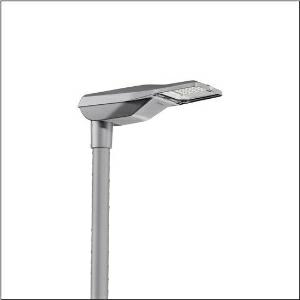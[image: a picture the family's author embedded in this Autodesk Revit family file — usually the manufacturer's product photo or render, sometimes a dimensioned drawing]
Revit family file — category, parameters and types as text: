
# Revit family: streetlight_sl_21_iq_micro___p0_8ab_5xe1r31d08db_6a63
name_source: partatom
category: Lighting Fixtures
units: mm (PartAtom-declared; Revit-internal decimal feet)

## family parameters
Cut with Voids When Loaded = No
Host = Face
Light Source = No
Part Type = Normal
Room Calculation Point = No
Round Connector Dimension = Use Diameter
Shared = No

## types (1)
- --- (1 x LED, 4220 lm, 36.4 W, 3000K)
    Apparent Load = 36 VA
    CIE Flux Codes = 36 71 98 100 100
    Color Rendering = 70
    Color Temperature = 3000K
    Default Elevation = 1800 mm
    Description = Streetlight SL 21 iQ micro, mast luminaire, primary light control with lens, of PMMA, primary optical cover: cover, of toughened safety glass, transparent, light distribution: P0.8aB, light emission: direct distribution, primary light characteristic: asymmetric, installation type: post-top, side-entry, LED, High Power LED, rated luminous flux: 4.220lm, luminous efficacy: 116lm/W, light colour: 730, colour temperature: 3000K, control gear: iQ-Comfort, control: pre-setting: linear dimming characteristic, Auto-Match, Temp-Guard, Lumen-Switch, Night-Set, Smart-Wire, Light-Fading, Desk-Remote (wireless, voltage-free reading and setting of iQ features in the workshop via application-optimized NFC function/RFID function), optimised constant luminous flux control (CLO 2.0), mains connection: 220..240V, AC, 50/60Hz, start of lifetime: 36W, end of service life: 38W, reduction: 16W, luminaire housing, of diecast aluminium, powder-coated, SITECO metallic grey (DB 702S), corrosivity category C5 high according to DIN EN ISO 12944, please order mast flange separately, inclination adjustable: 0°, 5°, 10°, 15°, sealing non-destructively replaceable, multi-level sealing system, length: 528mm, width: 235mm, height: 110mm, mast flange for spigot size: 42mm (side-entry): 5XC10008XM4, 60/48mm (side-entry/post-top): 5XC10108XM2, 76/60mm (side-entry/post-top): 5XC10108XM1, protection rating (complete): IP66, insulation class (complete): insulation class II (safety insulation), certification: CE, ENEC, ENEC+, VDE, impact resistance: IK10, permissible operating ambient temperature for outdoor applications: -40..+50°C, standard-compliant lighting for roads and squares, packaging unit: 1 piece

Light Distribution: P0.8aB
    Height = 110 mm
    Lamp = 1 x LED
    Lamp Light Flux = 4220 lm
    Lamp Power = 36.4 W
    Lamp count = 1
    Length = 528 mm
    Luminous efficacy = 116 lm/W
    Manufacturer = Siteco
    ModVariant = No
    Model = 5XE1R31D08DB
    Number of Poles = 1
    OnlyDefault = Yes
    Power Factor = 1
    Product Name = Streetlight SL 21 iQ micro | P0.8aB
    Product group = mast luminaire | pylon top
    ProductGroupID = 6100
    Protection Class = Protection class II
    Protection Degree = IP 66
    RLX_Detail_Level = 1
    RLX_Emergency_Light_Flux = 0 lm
    RLX_Emergency_Type = 0
    RLX_Emergency_Type_DB = No
    RlxData = <blob elided: 98685 chars, md5=c737e889>
    Socket = socket
    Standby Power = 0 W
    System Light Flux = 4220 lm
    System Power = 36 W
    Type Comments = factory setting: luminous flux: 100 % | dim-lin: 254 | 715 mA
    Type Image = l_1006881.jpg
    URL = http://relux.com
    VarID = @adj_082563
    Voltage = 0 V
    Weight = 0.00 kg
    Width = 235 mm

## geometry (parser evidence)
native form markers: Blend x4, Sweep x10
no freeform markers — native parametric forms only
